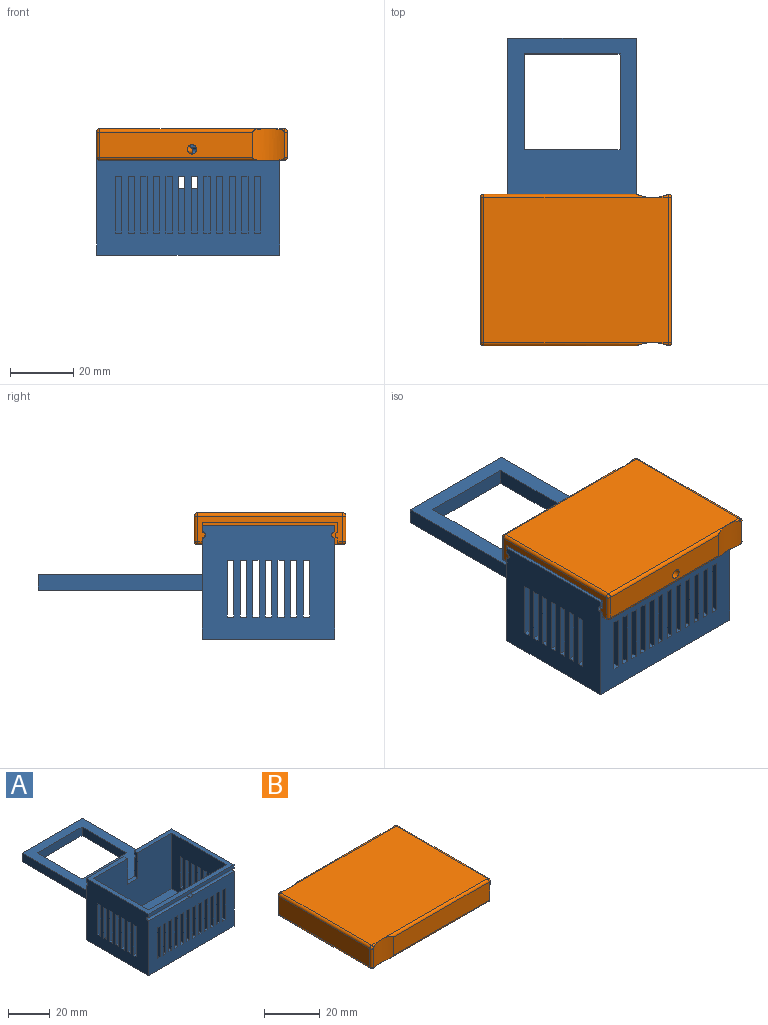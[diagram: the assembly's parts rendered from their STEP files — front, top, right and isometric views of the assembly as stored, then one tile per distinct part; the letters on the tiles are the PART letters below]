
ASSEMBLY  parts=2 mates=1
PART A: 135 faces, bbox 58x94x36 mm
  f0: plane 25.5x2mm, normal (0,1,0), area 51mm2, adj f2,f7,f37,f133
  f1: plane 58x32mm, normal (0,1,0), area 1575mm2, adj f2,f36,f37,f38,f39,f41,f42,f43
  f2: cylinder r=1mm len=25.5mm, axis (1,0,0), area 80.1mm2, adj f0,f1,f37,f133
  f3: plane 58x32mm, normal (0,-1,0), area 1423.3mm2, adj f5,f36,f37,f41,f50,f83,f84,f85
  f4: plane 58x2mm, normal (0,-1,0), area 115.3mm2, adj f5,f7,f36,f37,f50,f131
  f5: cylinder r=1mm len=27.93mm, axis (1,0,0), area 87.1mm2, adj f3,f4,f36,f131
  f6: plane 53x32.5mm, normal (0,1,0), area 1283.8mm2, adj f7,f80,f81,f82,f83,f84,f85,f86
  f7: plane 58x42mm, normal (0,0,1), area 457.5mm2, adj f0,f4,f6,f36,f37,f40,f79,f80
  f8: plane 2.5x2mm, normal (0,0,-1), area 5mm2, adj f9,f11,f37,f81
  f9: plane 18x2.5mm, normal (0,1,0), area 45mm2, adj f8,f10,f37,f81
  f10: plane 2.5x2mm, normal (0,0,1), area 5mm2, adj f9,f11,f37,f81
  f11: plane 18x2.5mm, normal (0,-1,0), area 45mm2, adj f8,f10,f37,f81
  f12: plane 2.5x2mm, normal (0,0,-1), area 5mm2, adj f13,f15,f37,f81
  f13: plane 18x2.5mm, normal (0,1,0), area 45mm2, adj f12,f14,f37,f81
  f14: plane 2.5x2mm, normal (0,0,1), area 5mm2, adj f13,f15,f37,f81
  f15: plane 18x2.5mm, normal (0,-1,0), area 45mm2, adj f12,f14,f37,f81
  f16: plane 2.5x2mm, normal (0,0,-1), area 5mm2, adj f17,f19,f37,f81
  f17: plane 18x2.5mm, normal (0,1,0), area 45mm2, adj f16,f18,f37,f81
  f18: plane 2.5x2mm, normal (0,0,1), area 5mm2, adj f17,f19,f37,f81
  f19: plane 18x2.5mm, normal (0,-1,0), area 45mm2, adj f16,f18,f37,f81
  f20: plane 2.5x2mm, normal (0,0,-1), area 5mm2, adj f21,f23,f37,f81
  f21: plane 18x2.5mm, normal (0,1,0), area 45mm2, adj f20,f22,f37,f81
  f22: plane 2.5x2mm, normal (0,0,1), area 5mm2, adj f21,f23,f37,f81
  f23: plane 18x2.5mm, normal (0,-1,0), area 45mm2, adj f20,f22,f37,f81
  f24: plane 2.5x2mm, normal (0,0,-1), area 5mm2, adj f25,f27,f37,f81
  f25: plane 18x2.5mm, normal (0,1,0), area 45mm2, adj f24,f26,f37,f81
  f26: plane 2.5x2mm, normal (0,0,1), area 5mm2, adj f25,f27,f37,f81
  f27: plane 18x2.5mm, normal (0,-1,0), area 45mm2, adj f24,f26,f37,f81
  f28: plane 2.5x2mm, normal (0,0,-1), area 5mm2, adj f29,f31,f37,f81
  f29: plane 18x2.5mm, normal (0,1,0), area 45mm2, adj f28,f30,f37,f81
  f30: plane 2.5x2mm, normal (0,0,1), area 5mm2, adj f29,f31,f37,f81
  f31: plane 18x2.5mm, normal (0,-1,0), area 45mm2, adj f28,f30,f37,f81
  f32: plane 2.5x2mm, normal (0,0,-1), area 5mm2, adj f33,f35,f37,f81
  f33: plane 18x2.5mm, normal (0,1,0), area 45mm2, adj f32,f34,f37,f81
  f34: plane 2.5x2mm, normal (0,0,1), area 5mm2, adj f33,f35,f37,f81
  f35: plane 18x2.5mm, normal (0,-1,0), area 45mm2, adj f32,f34,f37,f81
  f36: plane 42x36mm, normal (-1,0,0), area 1256.9mm2, adj f1,f3,f4,f5,f7,f40,f41,f49
  f37: plane 42x36mm, normal (1,0,0), area 1256.9mm2, adj f0,f1,f2,f3,f4,f7,f8,f9
  f38: plane 52x40.8mm, normal (0,0,1), area 1197.4mm2, adj f1,f42,f43,f44,f45,f46,f47,f48
  f39: plane 52x40.8mm, normal (0,0,-1), area 1197.4mm2, adj f1,f42,f43,f44,f45,f46,f47,f48
  f40: plane 25.5x2mm, normal (0,1,0), area 51mm2, adj f7,f36,f49,f132
  f41: plane 58x42mm, normal (0,0,-1), area 2436mm2, adj f1,f3,f36,f37
  f42: plane 52x5mm, normal (-1,0,0), area 260mm2, adj f1,f38,f39,f44
  f43: plane 52x5mm, normal (1,0,0), area 260mm2, adj f1,f38,f39,f44
  f44: plane 40.8x5mm, normal (0,1,0), area 204mm2, adj f38,f39,f42,f43
  f45: plane 30.4x5mm, normal (1,0,0), area 152mm2, adj f38,f39,f46,f48
  f46: plane 30.4x5mm, normal (0,1,0), area 152mm2, adj f38,f39,f45,f47
  f47: plane 30.4x5mm, normal (-1,0,0), area 152mm2, adj f38,f39,f46,f48
  f48: plane 30.4x5mm, normal (0,-1,0), area 152mm2, adj f38,f39,f45,f47
  f49: cylinder r=1mm len=25.5mm, axis (1,0,0), area 80.1mm2, adj f1,f36,f40,f132
  f50: cylinder r=1mm len=27.93mm, axis (1,0,0), area 87.1mm2, adj f3,f4,f37,f131
  f51: plane 2.5x2mm, normal (0,0,-1), area 5mm2, adj f36,f52,f54,f80
  f52: plane 18x2.5mm, normal (0,1,0), area 45mm2, adj f36,f51,f53,f80
  f53: plane 2.5x2mm, normal (0,0,1), area 5mm2, adj f36,f52,f54,f80
  f54: plane 18x2.5mm, normal (0,-1,0), area 45mm2, adj f36,f51,f53,f80
  f55: plane 2.5x2mm, normal (0,0,-1), area 5mm2, adj f36,f56,f58,f80
  f56: plane 18x2.5mm, normal (0,1,0), area 45mm2, adj f36,f55,f57,f80
  f57: plane 2.5x2mm, normal (0,0,1), area 5mm2, adj f36,f56,f58,f80
  f58: plane 18x2.5mm, normal (0,-1,0), area 45mm2, adj f36,f55,f57,f80
  f59: plane 2.5x2mm, normal (0,0,-1), area 5mm2, adj f36,f60,f62,f80
  f60: plane 18x2.5mm, normal (0,1,0), area 45mm2, adj f36,f59,f61,f80
  f61: plane 2.5x2mm, normal (0,0,1), area 5mm2, adj f36,f60,f62,f80
  f62: plane 18x2.5mm, normal (0,-1,0), area 45mm2, adj f36,f59,f61,f80
  f63: plane 2.5x2mm, normal (0,0,-1), area 5mm2, adj f36,f64,f66,f80
  f64: plane 18x2.5mm, normal (0,1,0), area 45mm2, adj f36,f63,f65,f80
  f65: plane 2.5x2mm, normal (0,0,1), area 5mm2, adj f36,f64,f66,f80
  f66: plane 18x2.5mm, normal (0,-1,0), area 45mm2, adj f36,f63,f65,f80
  f67: plane 2.5x2mm, normal (0,0,-1), area 5mm2, adj f36,f68,f70,f80
  f68: plane 18x2.5mm, normal (0,1,0), area 45mm2, adj f36,f67,f69,f80
  f69: plane 2.5x2mm, normal (0,0,1), area 5mm2, adj f36,f68,f70,f80
  f70: plane 18x2.5mm, normal (0,-1,0), area 45mm2, adj f36,f67,f69,f80
  f71: plane 2.5x2mm, normal (0,0,-1), area 5mm2, adj f36,f72,f74,f80
  f72: plane 18x2.5mm, normal (0,1,0), area 45mm2, adj f36,f71,f73,f80
  f73: plane 2.5x2mm, normal (0,0,1), area 5mm2, adj f36,f72,f74,f80
  f74: plane 18x2.5mm, normal (0,-1,0), area 45mm2, adj f36,f71,f73,f80
  f75: plane 2.5x2mm, normal (0,0,-1), area 5mm2, adj f36,f76,f78,f80
  f76: plane 18x2.5mm, normal (0,1,0), area 45mm2, adj f36,f75,f77,f80
  f77: plane 2.5x2mm, normal (0,0,1), area 5mm2, adj f36,f76,f78,f80
  f78: plane 18x2.5mm, normal (0,-1,0), area 45mm2, adj f36,f75,f77,f80
  f79: plane 53x32.5mm, normal (0,-1,0), area 1617.5mm2, adj f7,f80,f81,f82,f132,f133,f134
  f80: plane 37x32.5mm, normal (1,0,0), area 950.5mm2, adj f6,f7,f51,f52,f53,f54,f55,f56
  f81: plane 37x32.5mm, normal (-1,0,0), area 950.5mm2, adj f6,f7,f8,f9,f10,f11,f12,f13
  f82: plane 53x37mm, normal (0,0,1), area 1961mm2, adj f6,f79,f80,f81
  f83: plane 2.5x2mm, normal (0,0,-1), area 5mm2, adj f3,f6,f84,f86
  f84: plane 18x2.5mm, normal (1,0,0), area 45mm2, adj f3,f6,f83,f85
  f85: plane 2.5x2mm, normal (0,0,1), area 5mm2, adj f3,f6,f84,f86
  f86: plane 18x2.5mm, normal (-1,0,0), area 45mm2, adj f3,f6,f83,f85
  f87: plane 2.5x2mm, normal (0,0,-1), area 5mm2, adj f3,f6,f88,f90
  f88: plane 18x2.5mm, normal (1,0,0), area 45mm2, adj f3,f6,f87,f89
  f89: plane 2.5x2mm, normal (0,0,1), area 5mm2, adj f3,f6,f88,f90
  f90: plane 18x2.5mm, normal (-1,0,0), area 45mm2, adj f3,f6,f87,f89
  f91: plane 2.5x2mm, normal (0,0,-1), area 5mm2, adj f3,f6,f92,f94
  f92: plane 18x2.5mm, normal (1,0,0), area 45mm2, adj f3,f6,f91,f93
  f93: plane 2.5x2mm, normal (0,0,1), area 5mm2, adj f3,f6,f92,f94
  f94: plane 18x2.5mm, normal (-1,0,0), area 45mm2, adj f3,f6,f91,f93
  f95: plane 2.5x2mm, normal (0,0,-1), area 5mm2, adj f3,f6,f96,f98
  f96: plane 18x2.5mm, normal (1,0,0), area 45mm2, adj f3,f6,f95,f97
  f97: plane 2.5x2mm, normal (0,0,1), area 5mm2, adj f3,f6,f96,f98
  f98: plane 18x2.5mm, normal (-1,0,0), area 45mm2, adj f3,f6,f95,f97
  f99: plane 2.5x2mm, normal (0,0,-1), area 5mm2, adj f3,f6,f100,f102
  f100: plane 18x2.5mm, normal (1,0,0), area 45mm2, adj f3,f6,f99,f101
  f101: plane 2.5x2mm, normal (0,0,1), area 5mm2, adj f3,f6,f100,f102
  f102: plane 18x2.5mm, normal (-1,0,0), area 45mm2, adj f3,f6,f99,f101
  f103: plane 2.5x2mm, normal (0,0,-1), area 5mm2, adj f3,f6,f104,f106
  f104: plane 18x2.5mm, normal (1,0,0), area 45mm2, adj f3,f6,f103,f105
  f105: plane 2.5x2mm, normal (0,0,1), area 5mm2, adj f3,f6,f104,f106
  f106: plane 18x2.5mm, normal (-1,0,0), area 45mm2, adj f3,f6,f103,f105
  f107: plane 2.5x2mm, normal (0,0,-1), area 5mm2, adj f3,f6,f108,f110
  f108: plane 18x2.5mm, normal (1,0,0), area 45mm2, adj f3,f6,f107,f109
  f109: plane 2.5x2mm, normal (0,0,1), area 5mm2, adj f3,f6,f108,f110
  f110: plane 18x2.5mm, normal (-1,0,0), area 45mm2, adj f3,f6,f107,f109
  f111: plane 2.5x2mm, normal (0,0,-1), area 5mm2, adj f3,f6,f112,f114
  f112: plane 18x2.5mm, normal (1,0,0), area 45mm2, adj f3,f6,f111,f113
  f113: plane 2.5x2mm, normal (0,0,1), area 5mm2, adj f3,f6,f112,f114
  f114: plane 18x2.5mm, normal (-1,0,0), area 45mm2, adj f3,f6,f111,f113
  f115: plane 2.5x2mm, normal (0,0,-1), area 5mm2, adj f3,f6,f116,f118
  f116: plane 18x2.5mm, normal (1,0,0), area 45mm2, adj f3,f6,f115,f117
  f117: plane 2.5x2mm, normal (0,0,1), area 5mm2, adj f3,f6,f116,f118
  f118: plane 18x2.5mm, normal (-1,0,0), area 45mm2, adj f3,f6,f115,f117
  f119: plane 2.5x2mm, normal (0,0,-1), area 5mm2, adj f3,f6,f120,f122
  f120: plane 18x2.5mm, normal (1,0,0), area 45mm2, adj f3,f6,f119,f121
  f121: plane 2.5x2mm, normal (0,0,1), area 5mm2, adj f3,f6,f120,f122
  f122: plane 18x2.5mm, normal (-1,0,0), area 45mm2, adj f3,f6,f119,f121
  f123: plane 2.5x2mm, normal (0,0,-1), area 5mm2, adj f3,f6,f124,f126
  f124: plane 18x2.5mm, normal (1,0,0), area 45mm2, adj f3,f6,f123,f125
  f125: plane 2.5x2mm, normal (0,0,1), area 5mm2, adj f3,f6,f124,f126
  f126: plane 18x2.5mm, normal (-1,0,0), area 45mm2, adj f3,f6,f123,f125
  f127: plane 2.5x2mm, normal (0,0,-1), area 5mm2, adj f3,f6,f128,f130
  f128: plane 18x2.5mm, normal (1,0,0), area 45mm2, adj f3,f6,f127,f129
  f129: plane 2.5x2mm, normal (0,0,1), area 5mm2, adj f3,f6,f128,f130
  f130: plane 18x2.5mm, normal (-1,0,0), area 45mm2, adj f3,f6,f127,f129
  f131: cylinder r=1.46mm len=2.93mm, axis (0,-1,0), area 19.6mm2, adj f3,f4,f5,f6,f50
  f132: plane 15x2.5mm, normal (1,0,0), area 35.9mm2, adj f1,f7,f40,f49,f79,f134
  f133: plane 15x2.5mm, normal (-1,0,0), area 35.9mm2, adj f0,f1,f2,f7,f79,f134
  f134: plane 7x2.5mm, normal (0,0,1), area 17.5mm2, adj f1,f79,f132,f133
PART B: 43 faces, bbox 60.5x48x10 mm
  f0: cylinder r=1mm len=5mm, axis (-1,0,0), area 1.8mm2, adj f10,f22,f42
  f1: cylinder r=1mm len=53.5mm, axis (-1,0,0), area 78mm2, adj f10,f11,f28,f42
  f2: cylinder r=1mm len=53.5mm, axis (1,0,0), area 78mm2, adj f9,f11,f24,f42
  f3: cylinder r=1mm len=5mm, axis (1,0,0), area 1.8mm2, adj f9,f30,f42
  f4: cylinder r=1mm len=5mm, axis (1,0,0), area 1.8mm2, adj f10,f29,f41
  f5: cylinder r=1mm len=53.5mm, axis (-1,0,0), area 78mm2, adj f9,f12,f39,f41
  f6: cylinder r=0.9mm len=28.32mm, axis (1,0,0), area 78mm2, adj f7,f17,f18,f21
  f7: plane 59x3.1mm, normal (0,-1,0), area 180.7mm2, adj f6,f14,f15,f18,f20,f21
  f8: plane 59x3.1mm, normal (0,1,0), area 182.9mm2, adj f14,f15,f18,f19
  f9: plane 58.5x46mm, normal (0,0,-1), area 197mm2, adj f2,f3,f5,f16,f17,f18,f23,f34
  f10: plane 58.5x46mm, normal (0,0,1), area 2691mm2, adj f0,f1,f4,f26,f31,f32
  f11: plane 48.5x8mm, normal (0,-1,0), area 388mm2, adj f1,f2,f25,f42
  f12: plane 48.5x8mm, normal (0,1,0), area 381.3mm2, adj f5,f21,f32,f37,f41
  f13: plane 46x8mm, normal (-1,0,0), area 368mm2, adj f26,f27,f33,f34
  f14: plane 46x8mm, normal (1,0,0), area 112.5mm2, adj f7,f8,f15,f16,f17,f19,f20,f23
  f15: plane 59x43mm, normal (0,0,-1), area 2537mm2, adj f7,f8,f14,f18
  f16: plane 59x2.1mm, normal (0,1,0), area 123.7mm2, adj f9,f14,f18,f19,f23
  f17: plane 59x2.1mm, normal (0,-1,0), area 123.6mm2, adj f6,f9,f14,f18,f20,f21,f40
  f18: plane 43x7mm, normal (1,0,0), area 298.5mm2, adj f6,f7,f8,f9,f15,f16,f17,f19
  f19: cylinder r=0.9mm len=59mm, axis (1,0,0), area 166.8mm2, adj f8,f14,f16,f18
  f20: cylinder r=0.9mm len=29.82mm, axis (1,0,0), area 82.2mm2, adj f7,f14,f17,f21
  f21: cylinder r=1.46mm len=3.4mm, axis (0,1,0), area 26mm2, adj f6,f7,f12,f17,f20
  f22: sphere r=1mm, area 1.6mm2, adj f0,f26,f27
  f23: cylinder r=1mm len=1.5mm, axis (0,1,0), area 2.4mm2, adj f9,f14,f16,f24
  f24: sphere r=1mm, area 1.6mm2, adj f2,f23,f25
  f25: cylinder r=1mm len=8mm, axis (0,0,-1), area 12.6mm2, adj f11,f14,f24,f28
  f26: cylinder r=1mm len=46mm, axis (0,1,0), area 72.3mm2, adj f10,f13,f22,f29
  f27: cylinder r=1mm len=8mm, axis (0,0,1), area 12.6mm2, adj f13,f22,f30,f42
  f28: sphere r=1mm, area 1.6mm2, adj f1,f25,f31
  f29: sphere r=1mm, area 1.6mm2, adj f4,f26,f33
  f30: sphere r=1mm, area 1.6mm2, adj f3,f27,f34
  f31: cylinder r=1mm len=46mm, axis (0,-1,0), area 72.3mm2, adj f10,f14,f28,f35
  f32: cylinder r=1mm len=53.5mm, axis (1,0,0), area 78mm2, adj f10,f12,f35,f41
  f33: cylinder r=1mm len=8mm, axis (0,0,-1), area 12.6mm2, adj f13,f29,f36,f41
  f34: cylinder r=1mm len=46mm, axis (0,-1,0), area 72.3mm2, adj f9,f13,f30,f36
  f35: sphere r=1mm, area 1.6mm2, adj f31,f32,f37
  f36: sphere r=1mm, area 1.6mm2, adj f33,f34,f38
  f37: cylinder r=1mm len=8mm, axis (0,0,1), area 12.6mm2, adj f12,f14,f35,f39
  f38: cylinder r=1mm len=5mm, axis (-1,0,0), area 1.8mm2, adj f9,f36,f41
  f39: sphere r=1mm, area 1.6mm2, adj f5,f37,f40
  f40: cylinder r=1mm len=1.5mm, axis (0,1,0), area 2.4mm2, adj f9,f14,f17,f39
  f41: cylinder r=13mm len=10mm, axis (0,0,1), area 100mm2, adj f4,f5,f12,f32,f33,f38
  f42: cylinder r=13mm len=10mm, axis (0,0,1), area 100mm2, adj f0,f1,f2,f3,f11,f27
PLACE A t=(45.17,16.18,11.36)mm
PLACE B rot(axis=(0,0,-1),180deg) t=(16.17,15.68,46.36)mm
MATE slider B.f19 <-> A.f2  axis (-1,0,0) through (16.17,37.18,44.36)mm
